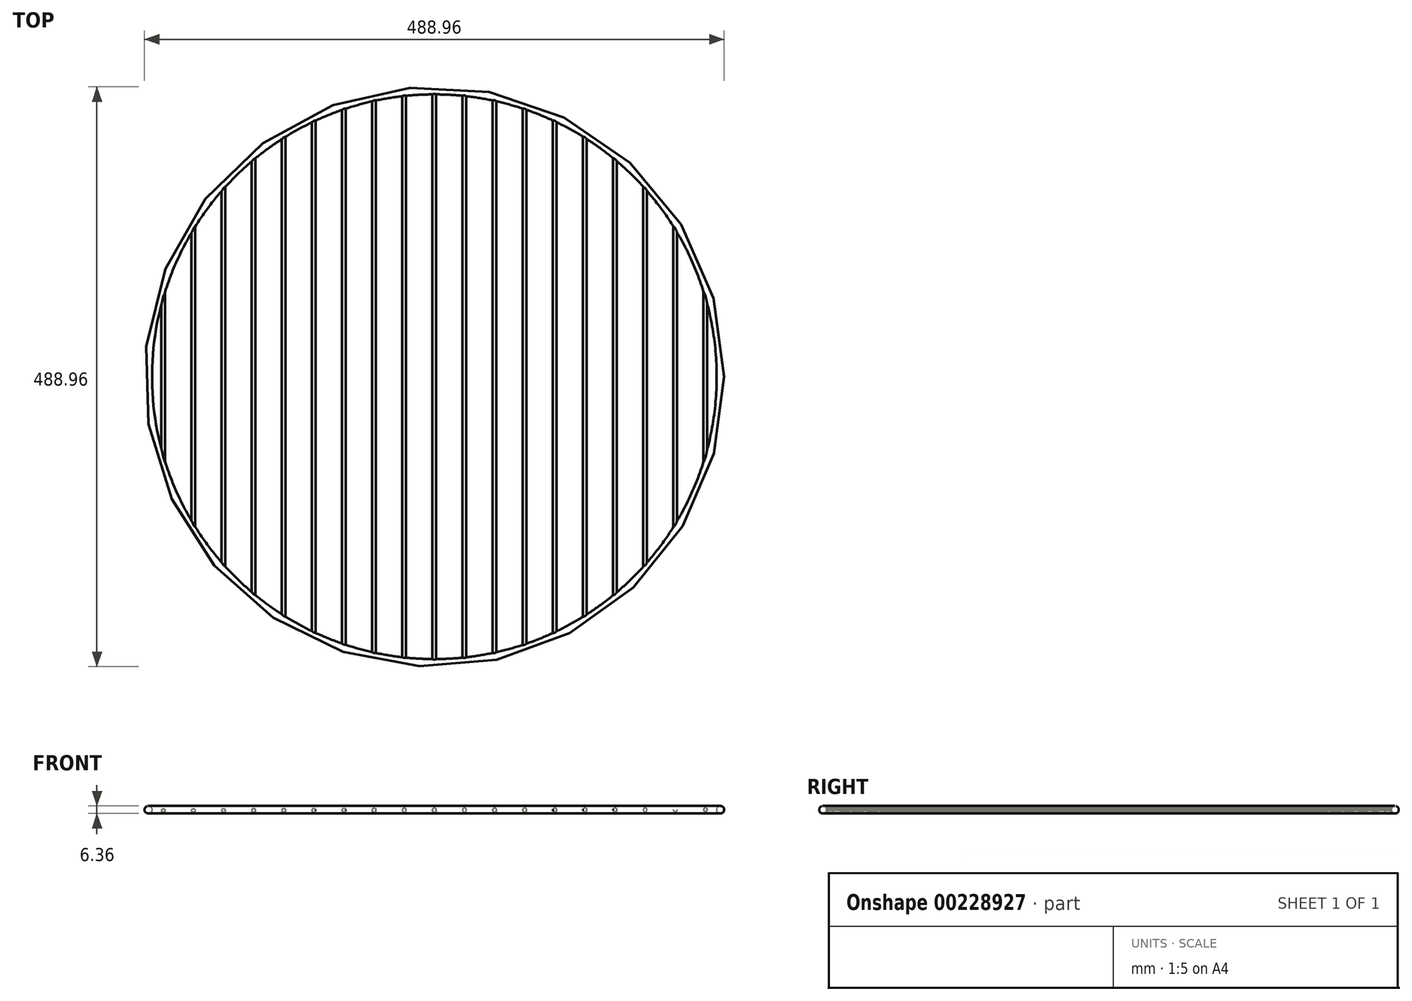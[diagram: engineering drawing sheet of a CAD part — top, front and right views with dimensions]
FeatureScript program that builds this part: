
annotation { "Feature Type Name" : "Feature", "Feature Type Description" : "" }
export const myFeature = defineFeature(function(context is Context, id is Id, definition is map)
    precondition{}
    {
        {
            var Q0;
            Q0=qCreatedBy(makeId("Front.planeOp"),FACE);
            var sketch = newSketch(context, id + "F0", { "sketchPlane" : qUnion([Q0])});
            skCircle(sketch, "E0", {"center": v(241.3, 0) * mm, "radius": 3.18 * mm});
            skLineSegment(sketch, "E1", {"start": v(0, 0) * mm, "end": v(0, 32.12) * mm, "construction": true});
            skSolve(sketch);
        }
        {
            var Q0;
            Q0=qCreatedBy(makeId("Front.planeOp"),FACE);
            var sketch = newSketch(context, id + "F1", { "sketchPlane" : qUnion([Q0])});
            skCircle(sketch, "E2", {"center": v(0, 0) * mm, "radius": 1.59 * mm});
            skCircle(sketch, "E3.0.1.0", {"center": v(-25.4, -0.08) * mm, "radius": 1.59 * mm});
            skCircle(sketch, "E3.0.2.0", {"center": v(-50.8, -0.15) * mm, "radius": 1.59 * mm});
            skCircle(sketch, "E3.0.3.0", {"center": v(-76.2, -0.23) * mm, "radius": 1.59 * mm});
            skCircle(sketch, "E3.0.4.0", {"center": v(-101.6, -0.3) * mm, "radius": 1.59 * mm});
            skCircle(sketch, "E3.0.5.0", {"center": v(-127, -0.38) * mm, "radius": 1.59 * mm});
            skCircle(sketch, "E3.0.6.0", {"center": v(-152.4, -0.46) * mm, "radius": 1.59 * mm});
            skCircle(sketch, "E3.0.7.0", {"center": v(-177.8, -0.53) * mm, "radius": 1.59 * mm});
            skCircle(sketch, "E3.0.8.0", {"center": v(-203.2, -0.61) * mm, "radius": 1.59 * mm});
            skCircle(sketch, "E3.0.9.0", {"center": v(-228.6, -0.69) * mm, "radius": 1.59 * mm});
            skCircle(sketch, "E3.1.0.0", {"center": v(25.4, 0) * mm, "radius": 1.59 * mm});
            skCircle(sketch, "E3.1.1.0", {"center": v(0, -0.08) * mm, "radius": 1.59 * mm});
            skCircle(sketch, "E3.1.2.0", {"center": v(-25.4, -0.15) * mm, "radius": 1.59 * mm});
            skCircle(sketch, "E3.1.3.0", {"center": v(-50.8, -0.23) * mm, "radius": 1.59 * mm});
            skCircle(sketch, "E3.1.4.0", {"center": v(-76.2, -0.3) * mm, "radius": 1.59 * mm});
            skCircle(sketch, "E3.1.5.0", {"center": v(-101.6, -0.38) * mm, "radius": 1.59 * mm});
            skCircle(sketch, "E3.1.6.0", {"center": v(-127, -0.46) * mm, "radius": 1.59 * mm});
            skCircle(sketch, "E3.1.7.0", {"center": v(-152.4, -0.53) * mm, "radius": 1.59 * mm});
            skCircle(sketch, "E3.1.8.0", {"center": v(-177.8, -0.61) * mm, "radius": 1.59 * mm});
            skCircle(sketch, "E3.1.9.0", {"center": v(-203.2, -0.69) * mm, "radius": 1.59 * mm});
            skCircle(sketch, "E3.2.0.0", {"center": v(50.8, 0) * mm, "radius": 1.59 * mm});
            skCircle(sketch, "E3.2.1.0", {"center": v(25.4, -0.08) * mm, "radius": 1.59 * mm});
            skCircle(sketch, "E3.2.2.0", {"center": v(0, -0.15) * mm, "radius": 1.59 * mm});
            skCircle(sketch, "E3.2.3.0", {"center": v(-25.4, -0.23) * mm, "radius": 1.59 * mm});
            skCircle(sketch, "E3.2.4.0", {"center": v(-50.8, -0.3) * mm, "radius": 1.59 * mm});
            skCircle(sketch, "E3.2.5.0", {"center": v(-76.2, -0.38) * mm, "radius": 1.59 * mm});
            skCircle(sketch, "E3.2.6.0", {"center": v(-101.6, -0.46) * mm, "radius": 1.59 * mm});
            skCircle(sketch, "E3.2.7.0", {"center": v(-127, -0.53) * mm, "radius": 1.59 * mm});
            skCircle(sketch, "E3.2.8.0", {"center": v(-152.4, -0.61) * mm, "radius": 1.59 * mm});
            skCircle(sketch, "E3.2.9.0", {"center": v(-177.8, -0.69) * mm, "radius": 1.59 * mm});
            skCircle(sketch, "E3.3.0.0", {"center": v(76.2, 0) * mm, "radius": 1.59 * mm});
            skCircle(sketch, "E3.3.1.0", {"center": v(50.8, -0.08) * mm, "radius": 1.59 * mm});
            skCircle(sketch, "E3.3.2.0", {"center": v(25.4, -0.15) * mm, "radius": 1.59 * mm});
            skCircle(sketch, "E3.3.3.0", {"center": v(0, -0.23) * mm, "radius": 1.59 * mm});
            skCircle(sketch, "E3.3.4.0", {"center": v(-25.4, -0.3) * mm, "radius": 1.59 * mm});
            skCircle(sketch, "E3.3.5.0", {"center": v(-50.8, -0.38) * mm, "radius": 1.59 * mm});
            skCircle(sketch, "E3.3.6.0", {"center": v(-76.2, -0.46) * mm, "radius": 1.59 * mm});
            skCircle(sketch, "E3.3.7.0", {"center": v(-101.6, -0.53) * mm, "radius": 1.59 * mm});
            skCircle(sketch, "E3.3.8.0", {"center": v(-127, -0.61) * mm, "radius": 1.59 * mm});
            skCircle(sketch, "E3.3.9.0", {"center": v(-152.4, -0.69) * mm, "radius": 1.59 * mm});
            skCircle(sketch, "E3.4.0.0", {"center": v(101.6, 0) * mm, "radius": 1.59 * mm});
            skCircle(sketch, "E3.4.1.0", {"center": v(76.2, -0.08) * mm, "radius": 1.59 * mm});
            skCircle(sketch, "E3.4.2.0", {"center": v(50.8, -0.15) * mm, "radius": 1.59 * mm});
            skCircle(sketch, "E3.4.3.0", {"center": v(25.4, -0.23) * mm, "radius": 1.59 * mm});
            skCircle(sketch, "E3.4.4.0", {"center": v(0, -0.3) * mm, "radius": 1.59 * mm});
            skCircle(sketch, "E3.4.5.0", {"center": v(-25.4, -0.38) * mm, "radius": 1.59 * mm});
            skCircle(sketch, "E3.4.6.0", {"center": v(-50.8, -0.46) * mm, "radius": 1.59 * mm});
            skCircle(sketch, "E3.4.7.0", {"center": v(-76.2, -0.53) * mm, "radius": 1.59 * mm});
            skCircle(sketch, "E3.4.8.0", {"center": v(-101.6, -0.61) * mm, "radius": 1.59 * mm});
            skCircle(sketch, "E3.4.9.0", {"center": v(-127, -0.69) * mm, "radius": 1.59 * mm});
            skCircle(sketch, "E3.5.0.0", {"center": v(127, 0) * mm, "radius": 1.59 * mm});
            skCircle(sketch, "E3.5.1.0", {"center": v(101.6, -0.08) * mm, "radius": 1.59 * mm});
            skCircle(sketch, "E3.5.2.0", {"center": v(76.2, -0.15) * mm, "radius": 1.59 * mm});
            skCircle(sketch, "E3.5.3.0", {"center": v(50.8, -0.23) * mm, "radius": 1.59 * mm});
            skCircle(sketch, "E3.5.4.0", {"center": v(25.4, -0.3) * mm, "radius": 1.59 * mm});
            skCircle(sketch, "E3.5.5.0", {"center": v(0, -0.38) * mm, "radius": 1.59 * mm});
            skCircle(sketch, "E3.5.6.0", {"center": v(-25.4, -0.46) * mm, "radius": 1.59 * mm});
            skCircle(sketch, "E3.5.7.0", {"center": v(-50.8, -0.53) * mm, "radius": 1.59 * mm});
            skCircle(sketch, "E3.5.8.0", {"center": v(-76.2, -0.61) * mm, "radius": 1.59 * mm});
            skCircle(sketch, "E3.5.9.0", {"center": v(-101.6, -0.69) * mm, "radius": 1.59 * mm});
            skCircle(sketch, "E3.6.0.0", {"center": v(152.4, 0) * mm, "radius": 1.59 * mm});
            skCircle(sketch, "E3.6.1.0", {"center": v(127, -0.08) * mm, "radius": 1.59 * mm});
            skCircle(sketch, "E3.6.2.0", {"center": v(101.6, -0.15) * mm, "radius": 1.59 * mm});
            skCircle(sketch, "E3.6.3.0", {"center": v(76.2, -0.23) * mm, "radius": 1.59 * mm});
            skCircle(sketch, "E3.6.4.0", {"center": v(50.8, -0.3) * mm, "radius": 1.59 * mm});
            skCircle(sketch, "E3.6.5.0", {"center": v(25.4, -0.38) * mm, "radius": 1.59 * mm});
            skCircle(sketch, "E3.6.6.0", {"center": v(0, -0.46) * mm, "radius": 1.59 * mm});
            skCircle(sketch, "E3.6.7.0", {"center": v(-25.4, -0.53) * mm, "radius": 1.59 * mm});
            skCircle(sketch, "E3.6.8.0", {"center": v(-50.8, -0.61) * mm, "radius": 1.59 * mm});
            skCircle(sketch, "E3.6.9.0", {"center": v(-76.2, -0.69) * mm, "radius": 1.59 * mm});
            skCircle(sketch, "E3.7.0.0", {"center": v(177.8, 0) * mm, "radius": 1.59 * mm});
            skCircle(sketch, "E3.7.1.0", {"center": v(152.4, -0.08) * mm, "radius": 1.59 * mm});
            skCircle(sketch, "E3.7.2.0", {"center": v(127, -0.15) * mm, "radius": 1.59 * mm});
            skCircle(sketch, "E3.7.3.0", {"center": v(101.6, -0.23) * mm, "radius": 1.59 * mm});
            skCircle(sketch, "E3.7.4.0", {"center": v(76.2, -0.3) * mm, "radius": 1.59 * mm});
            skCircle(sketch, "E3.7.5.0", {"center": v(50.8, -0.38) * mm, "radius": 1.59 * mm});
            skCircle(sketch, "E3.7.6.0", {"center": v(25.4, -0.46) * mm, "radius": 1.59 * mm});
            skCircle(sketch, "E3.7.7.0", {"center": v(0, -0.53) * mm, "radius": 1.59 * mm});
            skCircle(sketch, "E3.7.8.0", {"center": v(-25.4, -0.61) * mm, "radius": 1.59 * mm});
            skCircle(sketch, "E3.7.9.0", {"center": v(-50.8, -0.69) * mm, "radius": 1.59 * mm});
            skCircle(sketch, "E3.8.0.0", {"center": v(203.2, 0) * mm, "radius": 1.59 * mm});
            skCircle(sketch, "E3.8.1.0", {"center": v(177.8, -0.08) * mm, "radius": 1.59 * mm});
            skCircle(sketch, "E3.8.2.0", {"center": v(152.4, -0.15) * mm, "radius": 1.59 * mm});
            skCircle(sketch, "E3.8.3.0", {"center": v(127, -0.23) * mm, "radius": 1.59 * mm});
            skCircle(sketch, "E3.8.4.0", {"center": v(101.6, -0.3) * mm, "radius": 1.59 * mm});
            skCircle(sketch, "E3.8.5.0", {"center": v(76.2, -0.38) * mm, "radius": 1.59 * mm});
            skCircle(sketch, "E3.8.6.0", {"center": v(50.8, -0.46) * mm, "radius": 1.59 * mm});
            skCircle(sketch, "E3.8.7.0", {"center": v(25.4, -0.53) * mm, "radius": 1.59 * mm});
            skCircle(sketch, "E3.8.8.0", {"center": v(0, -0.61) * mm, "radius": 1.59 * mm});
            skCircle(sketch, "E3.8.9.0", {"center": v(-25.4, -0.69) * mm, "radius": 1.59 * mm});
            skCircle(sketch, "E3.9.0.0", {"center": v(228.6, 0) * mm, "radius": 1.59 * mm});
            skCircle(sketch, "E3.9.1.0", {"center": v(203.2, -0.08) * mm, "radius": 1.59 * mm});
            skCircle(sketch, "E3.9.2.0", {"center": v(177.8, -0.15) * mm, "radius": 1.59 * mm});
            skCircle(sketch, "E3.9.3.0", {"center": v(152.4, -0.23) * mm, "radius": 1.59 * mm});
            skCircle(sketch, "E3.9.4.0", {"center": v(127, -0.3) * mm, "radius": 1.59 * mm});
            skCircle(sketch, "E3.9.5.0", {"center": v(101.6, -0.38) * mm, "radius": 1.59 * mm});
            skCircle(sketch, "E3.9.6.0", {"center": v(76.2, -0.46) * mm, "radius": 1.59 * mm});
            skCircle(sketch, "E3.9.7.0", {"center": v(50.8, -0.53) * mm, "radius": 1.59 * mm});
            skCircle(sketch, "E3.9.8.0", {"center": v(25.4, -0.61) * mm, "radius": 1.59 * mm});
            skCircle(sketch, "E3.9.9.0", {"center": v(0, -0.69) * mm, "radius": 1.59 * mm});
            skLineSegment(sketch, "E3.direction1", {"start": v(0, 0) * mm, "end": v(25.4, 0) * mm, "construction": true});
            skLineSegment(sketch, "E3.direction2", {"start": v(0, 0) * mm, "end": v(-25.4, -0.08) * mm, "construction": true});
            skSolve(sketch);
        }
        {
            var Q0;
            Q0=makeQuery(id+"F0.imprint","IMPRINT",FACE,{"disambiguationData":[TD([[makeQuery(id+"F0.imprint","IMPRINT",EDGE,{"derivedFrom":sQuery(id+"F0.wireOp",EDGE,"E0")}),1.0]])]});
            var Q1;
            Q1=sQuery(id+"F0.wireOp",EDGE,"E1");
            revolve(context, id + "F2", {"entities" : qUnion([Q0]), "axis" : qUnion([Q1]), "revolveType" : RevolveType.FULL});
        }
        {
            var Q0;
            Q0 = qSketchRegion(id + "F1", true);
            extrude(context, id + "F3", {"entities" : qUnion([Q0]), "operationType" : NewBodyOperationType.ADD, "endBound" : BoundingType.UP_TO_NEXT, "depth" : 25.4 * mm, "hasSecondDirection" : true, "secondDirectionBound" : SecondDirectionBoundingType.UP_TO_NEXT, "secondDirectionOppositeDirection" : true, "secondDirectionDepth" : 25.4 * mm});
        }
    });
